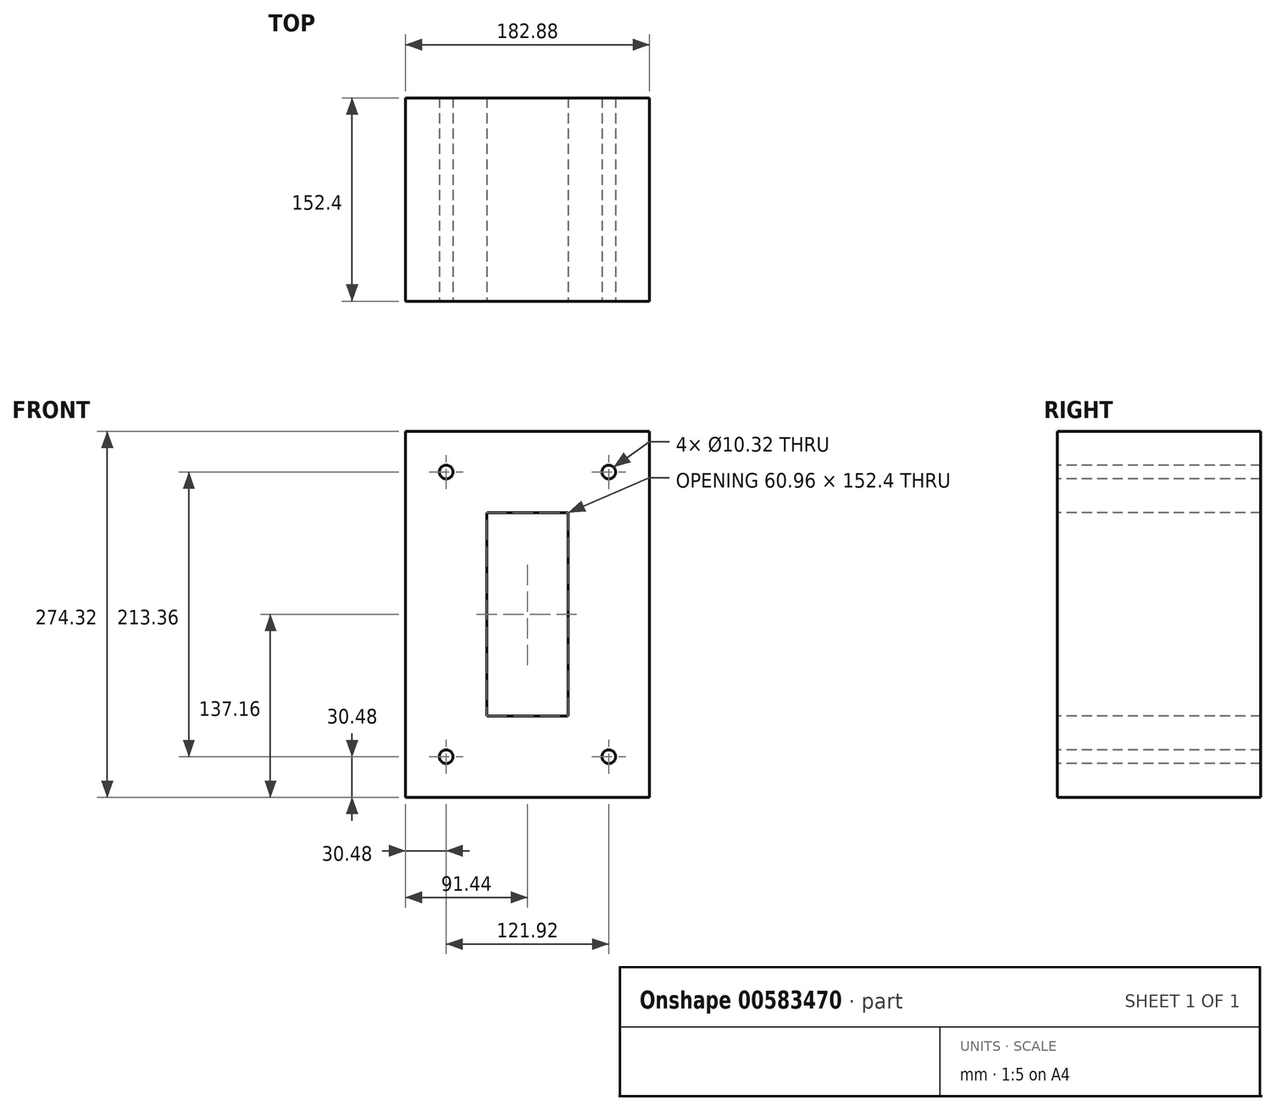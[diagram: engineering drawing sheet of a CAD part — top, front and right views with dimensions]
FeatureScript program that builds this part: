
annotation { "Feature Type Name" : "Feature", "Feature Type Description" : "" }
export const myFeature = defineFeature(function(context is Context, id is Id, definition is map)
    precondition{}
    {
        {
            assignVariable(context, id + "F0", {"name" : "Tongue", "anyValue" : 60.96 * mm});
        }
        {
            assignVariable(context, id + "F1", {"name" : "StackHeight", "anyValue" : 2.5 * getVariable(context, 'Tongue')});
        }
        {
            var Q0;
            Q0=qCreatedBy(makeId("Front.planeOp"),FACE);
            var sketch = newSketch(context, id + "F2", { "sketchPlane" : qUnion([Q0])});
            skLineSegment(sketch, "E0.bottom", {"start": v(91.44, -137.16) * mm, "end": v(-91.44, -137.16) * mm});
            skLineSegment(sketch, "E0.top", {"start": v(91.44, 137.16) * mm, "end": v(-91.44, 137.16) * mm});
            skLineSegment(sketch, "E0.left", {"start": v(91.44, -137.16) * mm, "end": v(91.44, 137.16) * mm});
            skLineSegment(sketch, "E0.right", {"start": v(-91.44, -137.16) * mm, "end": v(-91.44, 137.16) * mm});
            skPoint(sketch, "E0.middle", {"position": v(0, 0) * mm});
            skSolve(sketch);
        }
        {
            var Q0;
            Q0=qSketchRegion(id+"F2",true);
            extrude(context, id + "F3", {"entities" : qUnion([Q0]), "oppositeDirection" : true, "depth" : getVariable(context, 'StackHeight')});
        }
        {
            var Q0;
            Q0=makeQuery(id+"F3.opExtrude","CAP_FACE",FACE,{"disambiguationData":[OSD([sQuery(id+"F2.wireOp",EDGE,"E0.bottom"),sQuery(id+"F2.wireOp",EDGE,"E0.top"),sQuery(id+"F2.wireOp",EDGE,"E0.left"),sQuery(id+"F2.wireOp",EDGE,"E0.right")])],"isStart":true});
            var sketch = newSketch(context, id + "F4", { "sketchPlane" : qUnion([Q0])});
            skCircle(sketch, "E1", {"center": v(-60.96, 106.68) * mm, "radius": 5.16 * mm});
            skCircle(sketch, "E2", {"center": v(60.96, 106.68) * mm, "radius": 5.16 * mm});
            skCircle(sketch, "E3", {"center": v(-60.96, -106.68) * mm, "radius": 5.16 * mm});
            skCircle(sketch, "E4", {"center": v(60.96, -106.68) * mm, "radius": 5.16 * mm});
            skSolve(sketch);
        }
        {
            var Q0;
            Q0=qSketchRegion(id+"F4",true);
            extrude(context, id + "F5", {"entities" : qUnion([Q0]), "operationType" : NewBodyOperationType.REMOVE, "oppositeDirection" : true, "depth" : getVariable(context, 'StackHeight')});
        }
        {
            var Q0;
            Q0=makeQuery(id+"F3.opExtrude","CAP_FACE",FACE,{"disambiguationData":[OSD([sQuery(id+"F2.wireOp",EDGE,"E0.bottom"),sQuery(id+"F2.wireOp",EDGE,"E0.top"),sQuery(id+"F2.wireOp",EDGE,"E0.left"),sQuery(id+"F2.wireOp",EDGE,"E0.right")])],"isStart":true});
            var sketch = newSketch(context, id + "F6", { "sketchPlane" : qUnion([Q0])});
            skLineSegment(sketch, "E5.bottom", {"start": v(-30.48, -76.2) * mm, "end": v(30.48, -76.2) * mm});
            skLineSegment(sketch, "E5.top", {"start": v(-30.48, 76.2) * mm, "end": v(30.48, 76.2) * mm});
            skLineSegment(sketch, "E5.left", {"start": v(-30.48, -76.2) * mm, "end": v(-30.48, 76.2) * mm});
            skLineSegment(sketch, "E5.right", {"start": v(30.48, -76.2) * mm, "end": v(30.48, 76.2) * mm});
            skPoint(sketch, "E5.middle", {"position": v(0, 0) * mm});
            skSolve(sketch);
        }
        {
            var Q0;
            Q0=qSketchRegion(id+"F6",true);
            extrude(context, id + "F7", {"entities" : qUnion([Q0]), "operationType" : NewBodyOperationType.REMOVE, "oppositeDirection" : true, "depth" : getVariable(context, 'StackHeight')});
        }
        {
            var Q0;
            Q0=makeQuery(id+"F7.boolean.opBoolean","COPY",EDGE,{"derivedFrom":makeQuery(id+"F7.opExtrude","SWEPT_EDGE",EDGE,{"disambiguationData":[OSD([sQuery(id+"F6.wireOp",EDGE,"E5.top"),sQuery(id+"F6.wireOp",EDGE,"E5.left")])]})});
            var Q1;
            Q1=makeQuery(id+"F7.boolean.opBoolean","COPY",EDGE,{"derivedFrom":makeQuery(id+"F7.opExtrude","SWEPT_EDGE",EDGE,{"disambiguationData":[OSD([sQuery(id+"F6.wireOp",EDGE,"E5.top"),sQuery(id+"F6.wireOp",EDGE,"E5.right")])]})});
            var Q2;
            Q2=makeQuery(id+"F7.boolean.opBoolean","COPY",EDGE,{"derivedFrom":makeQuery(id+"F7.opExtrude","SWEPT_EDGE",EDGE,{"disambiguationData":[OSD([sQuery(id+"F6.wireOp",EDGE,"E5.bottom"),sQuery(id+"F6.wireOp",EDGE,"E5.right")])]})});
            var Q3;
            Q3=makeQuery(id+"F7.boolean.opBoolean","COPY",EDGE,{"derivedFrom":makeQuery(id+"F7.opExtrude","SWEPT_EDGE",EDGE,{"disambiguationData":[OSD([sQuery(id+"F6.wireOp",EDGE,"E5.bottom"),sQuery(id+"F6.wireOp",EDGE,"E5.left")])]})});
            fillet(context, id + "F8", {"entities" : qUnion([Q0, Q1, Q2, Q3]), "radius" : 0.8 * mm, "tangentPropagation" : true, "allowEdgeOverflow" : false});
        }
    });
